# Revit family: FOR UPDATE_72431XXX_new
name_source: partatom
category: Plumbing Fixtures
revit_build: Autodesk Revit 2018 (Build: 20170223_1515(x64)
units: mm (PartAtom-declared; Revit-internal decimal feet)

## family parameters
Always vertical = No
Cut with Voids When Loaded = No
OmniClass Number = 23.45.55.14
OmniClass Title = Single Faucets
Part Type = Normal
Room Calculation Point = No
Round Connector Dimension = Use Diameter
Shared = No
Work Plane-Based = Yes

## types (2) — shared parameters
Always visible = Yes
BIMobject category = Taps & Mixers
Default Elevation = 1219.2 mm  [stored 4 ft]
Description = Rebris E Bath spout
Design country = Germany
EAN code = 4059625412954
Edition number = 1
GTIN code = https://4059625412954
IFC Classification = Sanitary Terminal
Manufacturer = Hansgrohe
Manufacturer country = Germany
Manufacturer name = hansgrohe
Model = 72431XXX
OmniClass Code = 23-31 11 00
OmniClass Description = Faucets
Product Guid = 59b99651-fb40-4930-9aa0-3e760a0e094a
Product SKU = 72431XXX
Product data url = https://bimobject.com
Product family = Rebris E
Product group = Bath fillers
Product name = 72431XXX Rebris E Bath spout
QR code = https://bimobject.com
UNSPSC Code = 301815
URL = https://www.hansgrohe.com
Water Inlet = 13 mm
Water Inlet Description = Water Inlet 12.7mm
Weight Net (Kg) = 875

## per-type parameters (varying)
| type | Material 1 |
| 670 Matte Black | Hansgrohe - Metal - 670 Matte Black |
| 000 Chrome | Hansgrohe - Metal - 000 Chrome |

note: [stored X ft] marks values corroborated as IEEE doubles in the binary element streams (Revit-internal decimal feet)

## geometry (parser evidence)
native form markers: Sweep x1
no freeform markers — native parametric forms only
